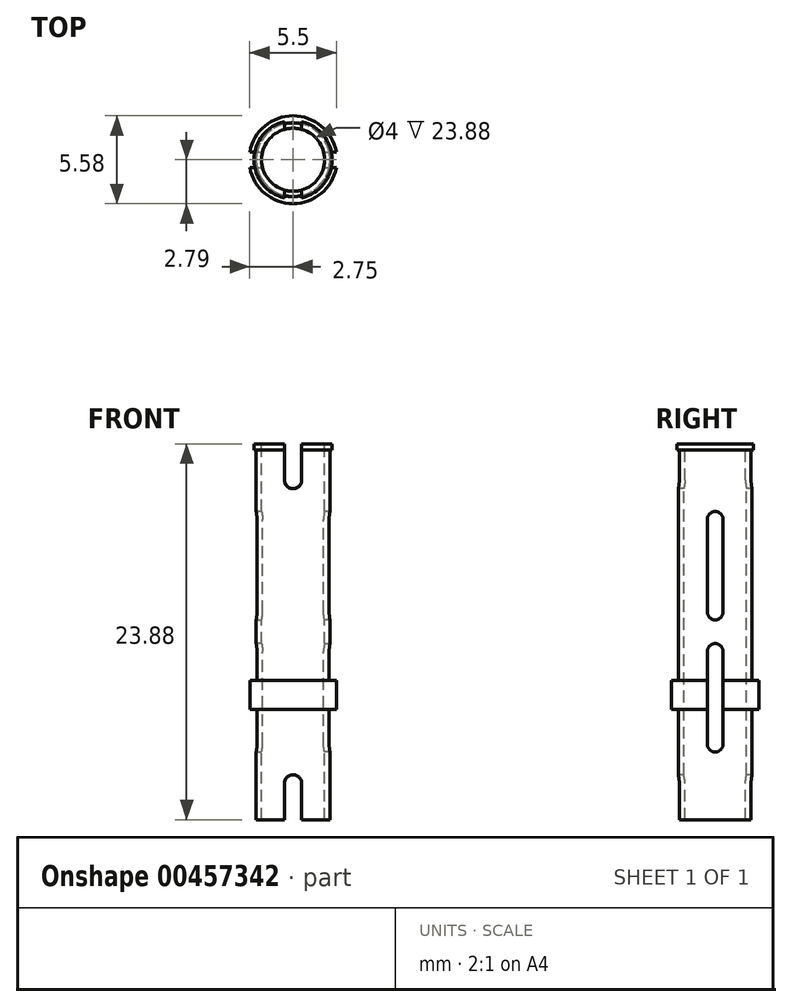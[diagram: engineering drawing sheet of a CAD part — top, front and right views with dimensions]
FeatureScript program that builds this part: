
annotation { "Feature Type Name" : "Feature", "Feature Type Description" : "" }
export const myFeature = defineFeature(function(context is Context, id is Id, definition is map)
    precondition{}
    {
        {
            var Q0;
            Q0=qCreatedBy(makeId("Top.planeOp"),FACE);
            var sketch = newSketch(context, id + "F0", { "sketchPlane" : qUnion([Q0])});
            skCircle(sketch, "E0", {"center": v(0, 0) * mm, "radius": 2.34 * mm});
            skSolve(sketch);
        }
        {
            var Q0;
            Q0 = qSketchRegion(id + "F0", true);
            extrude(context, id + "F1", {"entities" : qUnion([Q0]), "depth" : 11.94 * mm, "offsetDistance" : 25 * mm});
        }
        {
            var Q0;
            Q0 = qSketchRegion(id + "F0", true);
            extrude(context, id + "F2", {"entities" : qUnion([Q0]), "operationType" : NewBodyOperationType.ADD, "oppositeDirection" : true, "depth" : 11.94 * mm});
        }
        {
            var Q0;
            Q0=qCreatedBy(makeId("Front.planeOp"),FACE);
            var sketch = newSketch(context, id + "F3", { "sketchPlane" : qUnion([Q0])});
            skLineSegment(sketch, "E1.bottom", {"start": v(0.55, -12.96) * mm, "end": v(-0.54, -12.96) * mm});
            skLineSegment(sketch, "E1.top", {"start": v(0.55, -9.63) * mm, "end": v(-0.54, -9.63) * mm});
            skLineSegment(sketch, "E1.left", {"start": v(0.55, -12.96) * mm, "end": v(0.55, -9.63) * mm});
            skLineSegment(sketch, "E1.right", {"start": v(-0.54, -12.96) * mm, "end": v(-0.54, -9.63) * mm});
            skPoint(sketch, "E1.middle", {"position": v(0, -11.3) * mm});
            skCircle(sketch, "E2", {"center": v(0, -9.63) * mm, "radius": 0.54 * mm});
            skCircle(sketch, "E3.MirrorC", {"center": v(0, 9.63) * mm, "radius": 0.54 * mm});
            skLineSegment(sketch, "E4.MirrorCS", {"start": v(0.55, 12.96) * mm, "end": v(0.55, 9.63) * mm});
            skLineSegment(sketch, "E5.MirrorCS", {"start": v(-0.54, 12.96) * mm, "end": v(-0.54, 9.63) * mm});
            skLineSegment(sketch, "E6", {"start": v(-0.54, 12.96) * mm, "end": v(0.55, 12.96) * mm});
            skSolve(sketch);
        }
        {
            var Q0;
            Q0=qCreatedBy(makeId("Right.planeOp"),FACE);
            var sketch = newSketch(context, id + "F4", { "sketchPlane" : qUnion([Q0])});
            skLineSegment(sketch, "E7.bottom", {"start": v(0.5, -7.64) * mm, "end": v(-0.5, -7.64) * mm});
            skLineSegment(sketch, "E7.top", {"start": v(0.5, -0.75) * mm, "end": v(-0.5, -0.75) * mm});
            skLineSegment(sketch, "E7.left", {"start": v(0.5, -7.64) * mm, "end": v(0.5, -0.75) * mm});
            skLineSegment(sketch, "E7.right", {"start": v(-0.5, -7.64) * mm, "end": v(-0.5, -0.75) * mm});
            skPoint(sketch, "E7.middle", {"position": v(0, -4.2) * mm});
            skLineSegment(sketch, "E8.MirrorCS", {"start": v(0.5, 0.75) * mm, "end": v(-0.5, 0.75) * mm});
            skLineSegment(sketch, "E9.MirrorCS", {"start": v(-0.5, 7.64) * mm, "end": v(-0.5, 0.75) * mm});
            skLineSegment(sketch, "E10.MirrorCS", {"start": v(0.5, 7.64) * mm, "end": v(0.5, 0.75) * mm});
            skLineSegment(sketch, "E11.MirrorCS", {"start": v(0.5, 7.64) * mm, "end": v(-0.5, 7.64) * mm});
            skSolve(sketch);
        }
        {
            var Q0;
            Q0 = qSketchRegion(id + "F3", true);
            extrude(context, id + "F5", {"entities" : qUnion([Q0]), "operationType" : NewBodyOperationType.REMOVE, "oppositeDirection" : true, "depth" : 333 * mm, "symmetric" : true});
        }
        {
            var Q0;
            Q0 = qSketchRegion(id + "F3", true);
            extrude(context, id + "F6", {"entities" : qUnion([Q0]), "operationType" : NewBodyOperationType.REMOVE, "oppositeDirection" : true, "depth" : 25 * mm, "symmetric" : true});
        }
        {
            var Q0;
            Q0=qCreatedBy(makeId("Front.planeOp"),FACE);
            var sketch = newSketch(context, id + "F7", { "sketchPlane" : qUnion([Q0])});
            skLineSegment(sketch, "E12.bottom", {"start": v(-2.3, -3.08) * mm, "end": v(-2.8, -3.08) * mm});
            skLineSegment(sketch, "E12.top", {"start": v(-2.3, -4.94) * mm, "end": v(-2.8, -4.94) * mm});
            skLineSegment(sketch, "E12.left", {"start": v(-2.3, -3.08) * mm, "end": v(-2.3, -4.94) * mm});
            skLineSegment(sketch, "E12.right", {"start": v(-2.8, -3.08) * mm, "end": v(-2.8, -4.94) * mm});
            skSolve(sketch);
        }
        {
            var Q0;
            Q0 = qSketchRegion(id + "F7", true);
            var Q1;
            {var subQ0=sQuery(id+"F0.wireOp",EDGE,"E0");Q1=makeQuery(id+"F2.boolean.opBoolean","MERGE",FACE,{"derivedFrom":[makeQuery(id+"F1.opExtrude","SWEPT_FACE",FACE,{"disambiguationData":[OSD([subQ0])]}),makeQuery(id+"F2.opExtrude","SWEPT_FACE",FACE,{"disambiguationData":[OSD([subQ0])]})]});}
            revolve(context, id + "F8", {"operationType" : NewBodyOperationType.ADD, "entities" : qUnion([Q0]), "axis" : qUnion([Q1]), "revolveType" : RevolveType.FULL});
        }
        {
            var Q0;
            Q0 = qSketchRegion(id + "F4", true);
            extrude(context, id + "F9", {"entities" : qUnion([Q0]), "operationType" : NewBodyOperationType.REMOVE, "oppositeDirection" : true, "depth" : 25 * mm, "symmetric" : true});
        }
        {
            var Q0;
            Q0=qCreatedBy(makeId("Top.planeOp"),FACE);
            var sketch = newSketch(context, id + "F10", { "sketchPlane" : qUnion([Q0])});
            skCircle(sketch, "E13", {"center": v(0, 0) * mm, "radius": 2 * mm});
            skSolve(sketch);
        }
        {
            var Q0;
            Q0 = qSketchRegion(id + "F10", true);
            extrude(context, id + "F11", {"entities" : qUnion([Q0]), "operationType" : NewBodyOperationType.REMOVE, "oppositeDirection" : true, "depth" : 41 * mm, "symmetric" : true});
        }
        {
            var Q0;
            Q0=qCreatedBy(makeId("Right.planeOp"),FACE);
            var sketch = newSketch(context, id + "F12", { "sketchPlane" : qUnion([Q0])});
            skLineSegment(sketch, "E14.bottom", {"start": v(2.28, 11.94) * mm, "end": v(2.48, 11.94) * mm});
            skLineSegment(sketch, "E14.top", {"start": v(2.28, 11.54) * mm, "end": v(2.48, 11.54) * mm});
            skLineSegment(sketch, "E14.left", {"start": v(2.28, 11.94) * mm, "end": v(2.28, 11.54) * mm});
            skLineSegment(sketch, "E14.right", {"start": v(2.48, 11.94) * mm, "end": v(2.48, 11.54) * mm});
            skSolve(sketch);
        }
        {
            var Q0;
            Q0 = qSketchRegion(id + "F12", true);
            var Q1;
            {var subQ0=sQuery(id+"F0.wireOp",EDGE,"E0");Q1=makeQuery(id+"F8.boolean.opBoolean","SPLIT",FACE,{"disambiguationData":[TD([makeQuery(id+"F1.opExtrude","CAP_FACE",FACE,{"disambiguationData":[OSD([subQ0])],"isStart":false})])],"derivedFrom":makeQuery(id+"F2.boolean.opBoolean","MERGE",FACE,{"derivedFrom":[makeQuery(id+"F1.opExtrude","SWEPT_FACE",FACE,{"disambiguationData":[OSD([subQ0])]}),makeQuery(id+"F2.opExtrude","SWEPT_FACE",FACE,{"disambiguationData":[OSD([subQ0])]})]})});}
            revolve(context, id + "F13", {"operationType" : NewBodyOperationType.ADD, "entities" : qUnion([Q0]), "axis" : qUnion([Q1]), "revolveType" : RevolveType.FULL});
        }
        {
            var Q0;
            Q0 = qSketchRegion(id + "F3", true);
            extrude(context, id + "F14", {"entities" : qUnion([Q0]), "operationType" : NewBodyOperationType.REMOVE, "oppositeDirection" : true, "depth" : 25 * mm, "symmetric" : true});
        }
        {
            var Q0;
            Q0 = qSketchRegion(id + "F3", true);
            extrude(context, id + "F15", {"entities" : qUnion([Q0]), "operationType" : NewBodyOperationType.REMOVE, "oppositeDirection" : true, "depth" : 25 * mm});
        }
        {
            var Q0;
            Q0 = qSketchRegion(id + "F3", true);
            extrude(context, id + "F16", {"entities" : qUnion([Q0]), "operationType" : NewBodyOperationType.REMOVE, "oppositeDirection" : true, "depth" : 25 * mm, "symmetric" : true});
        }
        {
            var Q0;
            Q0=makeQuery(id+"F11.boolean.opBoolean","SPLIT",EDGE,{"disambiguationData":[OD(1.0)],"derivedFrom":makeQuery(id+"F9.boolean.opBoolean","COPY",EDGE,{"derivedFrom":makeQuery(id+"F9.opExtrude","SWEPT_EDGE",EDGE,{"disambiguationData":[OSD([sQuery(id+"F4.wireOp",EDGE,"E8.MirrorCS"),sQuery(id+"F4.wireOp",EDGE,"E10.MirrorCS")])]})})});
            var Q1;
            Q1=makeQuery(id+"F11.boolean.opBoolean","SPLIT",EDGE,{"disambiguationData":[OD(1.0)],"derivedFrom":makeQuery(id+"F9.boolean.opBoolean","COPY",EDGE,{"derivedFrom":makeQuery(id+"F9.opExtrude","SWEPT_EDGE",EDGE,{"disambiguationData":[OSD([sQuery(id+"F4.wireOp",EDGE,"E8.MirrorCS"),sQuery(id+"F4.wireOp",EDGE,"E9.MirrorCS")])]})})});
            var Q2;
            Q2=makeQuery(id+"F11.boolean.opBoolean","SPLIT",EDGE,{"disambiguationData":[OD(1.0)],"derivedFrom":makeQuery(id+"F9.boolean.opBoolean","COPY",EDGE,{"derivedFrom":makeQuery(id+"F9.opExtrude","SWEPT_EDGE",EDGE,{"disambiguationData":[OSD([sQuery(id+"F4.wireOp",EDGE,"E7.top"),sQuery(id+"F4.wireOp",EDGE,"E7.right")])]})})});
            var Q3;
            Q3=makeQuery(id+"F11.boolean.opBoolean","SPLIT",EDGE,{"disambiguationData":[OD(1.0)],"derivedFrom":makeQuery(id+"F9.boolean.opBoolean","COPY",EDGE,{"derivedFrom":makeQuery(id+"F9.opExtrude","SWEPT_EDGE",EDGE,{"disambiguationData":[OSD([sQuery(id+"F4.wireOp",EDGE,"E7.top"),sQuery(id+"F4.wireOp",EDGE,"E7.left")])]})})});
            var Q4;
            Q4=makeQuery(id+"F11.boolean.opBoolean","SPLIT",EDGE,{"disambiguationData":[OD(1.0)],"derivedFrom":makeQuery(id+"F9.boolean.opBoolean","COPY",EDGE,{"derivedFrom":makeQuery(id+"F9.opExtrude","SWEPT_EDGE",EDGE,{"disambiguationData":[OSD([sQuery(id+"F4.wireOp",EDGE,"E7.bottom"),sQuery(id+"F4.wireOp",EDGE,"E7.right")])]})})});
            var Q5;
            Q5=makeQuery(id+"F11.boolean.opBoolean","SPLIT",EDGE,{"disambiguationData":[OD(1.0)],"derivedFrom":makeQuery(id+"F9.boolean.opBoolean","COPY",EDGE,{"derivedFrom":makeQuery(id+"F9.opExtrude","SWEPT_EDGE",EDGE,{"disambiguationData":[OSD([sQuery(id+"F4.wireOp",EDGE,"E7.bottom"),sQuery(id+"F4.wireOp",EDGE,"E7.left")])]})})});
            var Q6;
            Q6=makeQuery(id+"F11.boolean.opBoolean","SPLIT",EDGE,{"disambiguationData":[OD(1.0)],"derivedFrom":makeQuery(id+"F9.boolean.opBoolean","COPY",EDGE,{"derivedFrom":makeQuery(id+"F9.opExtrude","SWEPT_EDGE",EDGE,{"disambiguationData":[OSD([sQuery(id+"F4.wireOp",EDGE,"E9.MirrorCS"),sQuery(id+"F4.wireOp",EDGE,"E11.MirrorCS")])]})})});
            var Q7;
            Q7=makeQuery(id+"F11.boolean.opBoolean","SPLIT",EDGE,{"disambiguationData":[OD(1.0)],"derivedFrom":makeQuery(id+"F9.boolean.opBoolean","COPY",EDGE,{"derivedFrom":makeQuery(id+"F9.opExtrude","SWEPT_EDGE",EDGE,{"disambiguationData":[OSD([sQuery(id+"F4.wireOp",EDGE,"E10.MirrorCS"),sQuery(id+"F4.wireOp",EDGE,"E11.MirrorCS")])]})})});
            var Q8;
            Q8=makeQuery(id+"F11.boolean.opBoolean","SPLIT",EDGE,{"disambiguationData":[OD(0.0)],"derivedFrom":makeQuery(id+"F9.boolean.opBoolean","COPY",EDGE,{"derivedFrom":makeQuery(id+"F9.opExtrude","SWEPT_EDGE",EDGE,{"disambiguationData":[OSD([sQuery(id+"F4.wireOp",EDGE,"E9.MirrorCS"),sQuery(id+"F4.wireOp",EDGE,"E11.MirrorCS")])]})})});
            var Q9;
            Q9=makeQuery(id+"F11.boolean.opBoolean","SPLIT",EDGE,{"disambiguationData":[OD(0.0)],"derivedFrom":makeQuery(id+"F9.boolean.opBoolean","COPY",EDGE,{"derivedFrom":makeQuery(id+"F9.opExtrude","SWEPT_EDGE",EDGE,{"disambiguationData":[OSD([sQuery(id+"F4.wireOp",EDGE,"E10.MirrorCS"),sQuery(id+"F4.wireOp",EDGE,"E11.MirrorCS")])]})})});
            var Q10;
            Q10=makeQuery(id+"F11.boolean.opBoolean","SPLIT",EDGE,{"disambiguationData":[OD(0.0)],"derivedFrom":makeQuery(id+"F9.boolean.opBoolean","COPY",EDGE,{"derivedFrom":makeQuery(id+"F9.opExtrude","SWEPT_EDGE",EDGE,{"disambiguationData":[OSD([sQuery(id+"F4.wireOp",EDGE,"E8.MirrorCS"),sQuery(id+"F4.wireOp",EDGE,"E9.MirrorCS")])]})})});
            var Q11;
            Q11=makeQuery(id+"F11.boolean.opBoolean","SPLIT",EDGE,{"disambiguationData":[OD(0.0)],"derivedFrom":makeQuery(id+"F9.boolean.opBoolean","COPY",EDGE,{"derivedFrom":makeQuery(id+"F9.opExtrude","SWEPT_EDGE",EDGE,{"disambiguationData":[OSD([sQuery(id+"F4.wireOp",EDGE,"E8.MirrorCS"),sQuery(id+"F4.wireOp",EDGE,"E10.MirrorCS")])]})})});
            var Q12;
            Q12=makeQuery(id+"F11.boolean.opBoolean","SPLIT",EDGE,{"disambiguationData":[OD(0.0)],"derivedFrom":makeQuery(id+"F9.boolean.opBoolean","COPY",EDGE,{"derivedFrom":makeQuery(id+"F9.opExtrude","SWEPT_EDGE",EDGE,{"disambiguationData":[OSD([sQuery(id+"F4.wireOp",EDGE,"E7.bottom"),sQuery(id+"F4.wireOp",EDGE,"E7.left")])]})})});
            var Q13;
            Q13=makeQuery(id+"F11.boolean.opBoolean","SPLIT",EDGE,{"disambiguationData":[OD(0.0)],"derivedFrom":makeQuery(id+"F9.boolean.opBoolean","COPY",EDGE,{"derivedFrom":makeQuery(id+"F9.opExtrude","SWEPT_EDGE",EDGE,{"disambiguationData":[OSD([sQuery(id+"F4.wireOp",EDGE,"E7.bottom"),sQuery(id+"F4.wireOp",EDGE,"E7.right")])]})})});
            var Q14;
            Q14=makeQuery(id+"F11.boolean.opBoolean","SPLIT",EDGE,{"disambiguationData":[OD(0.0)],"derivedFrom":makeQuery(id+"F9.boolean.opBoolean","COPY",EDGE,{"derivedFrom":makeQuery(id+"F9.opExtrude","SWEPT_EDGE",EDGE,{"disambiguationData":[OSD([sQuery(id+"F4.wireOp",EDGE,"E7.top"),sQuery(id+"F4.wireOp",EDGE,"E7.left")])]})})});
            var Q15;
            Q15=makeQuery(id+"F11.boolean.opBoolean","SPLIT",EDGE,{"disambiguationData":[OD(0.0)],"derivedFrom":makeQuery(id+"F9.boolean.opBoolean","COPY",EDGE,{"derivedFrom":makeQuery(id+"F9.opExtrude","SWEPT_EDGE",EDGE,{"disambiguationData":[OSD([sQuery(id+"F4.wireOp",EDGE,"E7.top"),sQuery(id+"F4.wireOp",EDGE,"E7.right")])]})})});
            fillet(context, id + "F17", {"entities" : qUnion([Q0, Q1, Q2, Q3, Q4, Q5, Q6, Q7, Q8, Q9, Q10, Q11, Q12, Q13, Q14, Q15]), "radius" : 0.5 * mm, "tangentPropagation" : true, "allowEdgeOverflow" : false});
        }
    });
